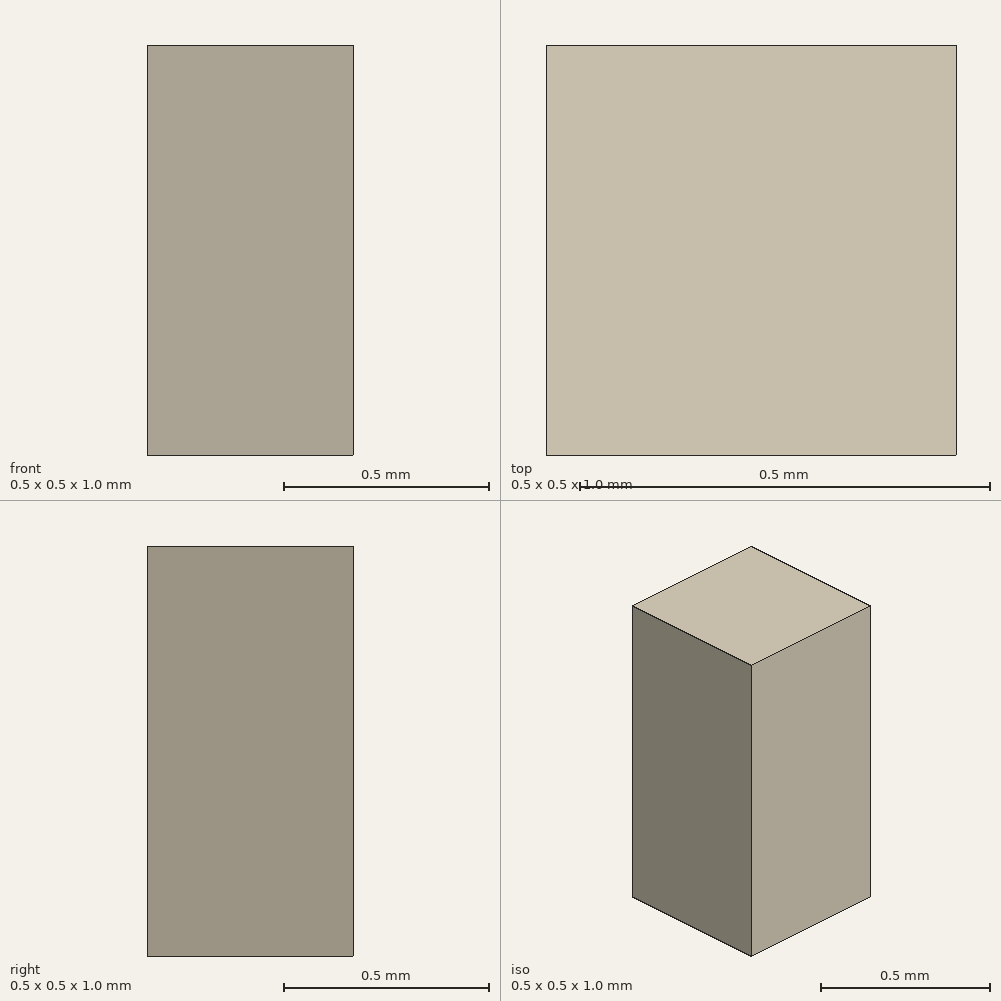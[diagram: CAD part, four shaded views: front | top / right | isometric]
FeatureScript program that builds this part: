
annotation { "Feature Type Name" : "Feature", "Feature Type Description" : "" }
export const myFeature = defineFeature(function(context is Context, id is Id, definition is map)
    precondition{}
    {
        {
            var Q0;
            Q0=qCreatedBy(makeId("Top.planeOp"),FACE);
            var sketch = newSketch(context, id + "F0", { "sketchPlane" : qUnion([Q0])});
            skLineSegment(sketch, "E0.bottom", {"start": v(0.25, -0.25) * mm, "end": v(-0.25, -0.25) * mm});
            skLineSegment(sketch, "E0.top", {"start": v(0.25, 0.25) * mm, "end": v(-0.25, 0.25) * mm});
            skLineSegment(sketch, "E0.left", {"start": v(0.25, -0.25) * mm, "end": v(0.25, 0.25) * mm});
            skLineSegment(sketch, "E0.right", {"start": v(-0.25, -0.25) * mm, "end": v(-0.25, 0.25) * mm});
            skPoint(sketch, "E0.middle", {"position": v(0, 0) * mm});
            skSolve(sketch);
        }
        {
            var Q0;
            Q0=makeQuery(id+"F0.imprint","IMPRINT",FACE,{"disambiguationData":[TD([[makeQuery(id+"F0.imprint","IMPRINT",EDGE,{"derivedFrom":sQuery(id+"F0.wireOp",EDGE,"E0.bottom")}),-1.0]])]});
            extrude(context, id + "F1", {"entities" : qUnion([Q0]), "depth" : 1 * mm, "offsetDistance" : 25 * mm});
        }
    });
